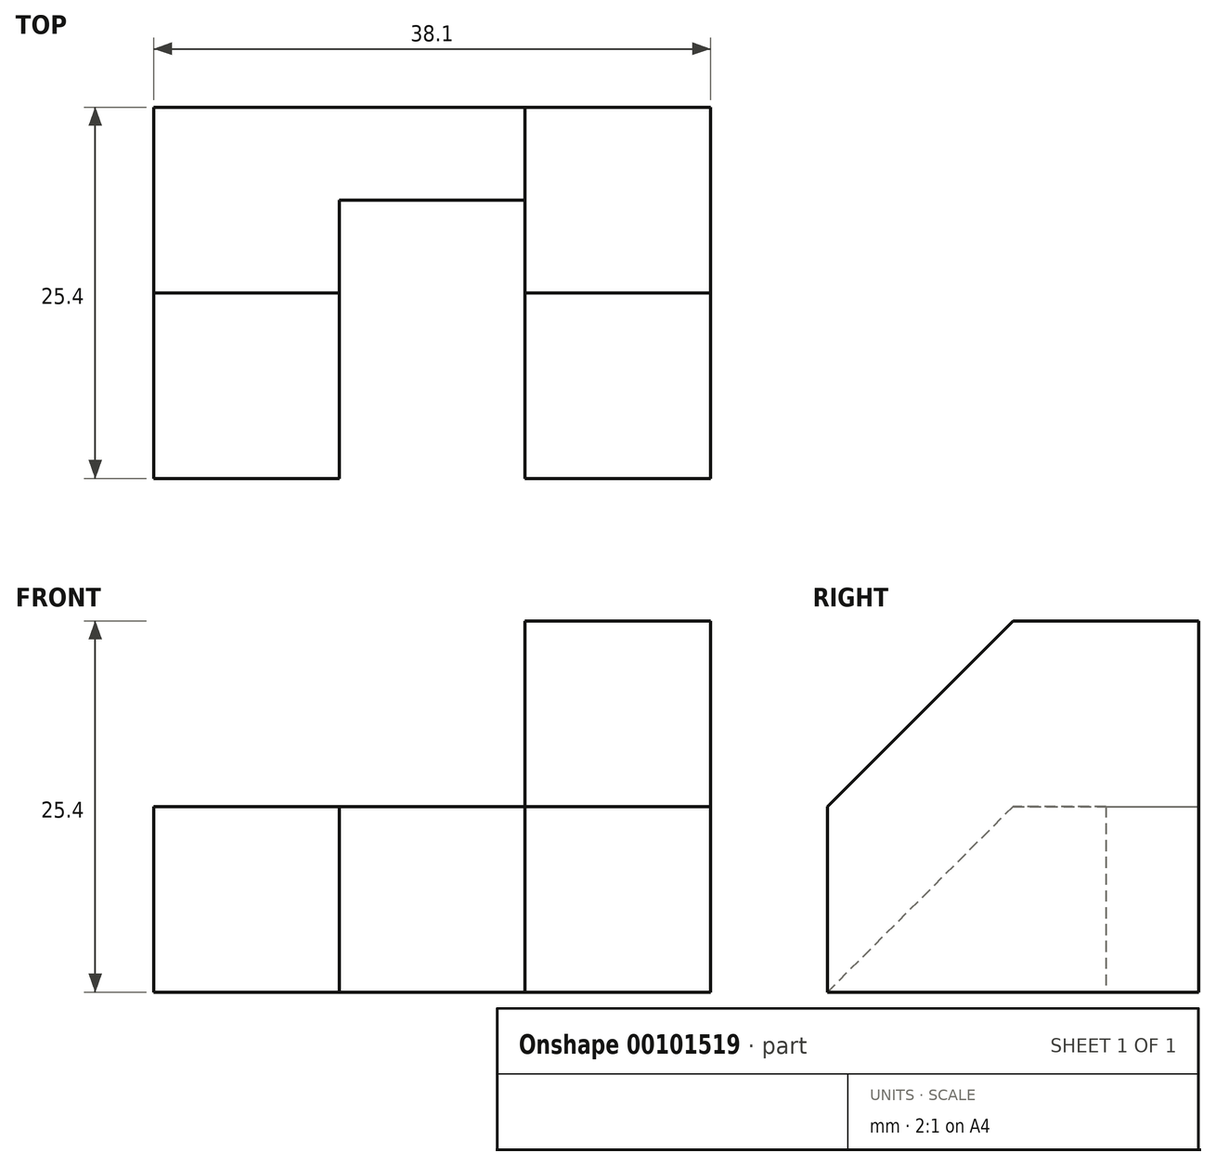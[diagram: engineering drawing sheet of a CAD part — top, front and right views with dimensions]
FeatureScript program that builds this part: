
annotation { "Feature Type Name" : "Feature", "Feature Type Description" : "" }
export const myFeature = defineFeature(function(context is Context, id is Id, definition is map)
    precondition{}
    {
        {
            var Q0;
            Q0=qCreatedBy(makeId("Top.planeOp"),FACE);
            var sketch = newSketch(context, id + "F0", { "sketchPlane" : qUnion([Q0])});
            skLineSegment(sketch, "E0.bottom", {"start": v(0, 0) * mm, "end": v(38.1, 0) * mm});
            skLineSegment(sketch, "E0.top", {"start": v(0, -25.4) * mm, "end": v(38.1, -25.4) * mm});
            skLineSegment(sketch, "E0.left", {"start": v(0, 0) * mm, "end": v(0, -25.4) * mm});
            skLineSegment(sketch, "E0.right", {"start": v(38.1, 0) * mm, "end": v(38.1, -25.4) * mm});
            skSolve(sketch);
        }
        {
            var Q0;
            Q0 = qSketchRegion(id + "F0", true);
            extrude(context, id + "F1", {"entities" : qUnion([Q0]), "depth" : 25.4 * mm});
        }
        {
            var Q0;
            Q0=qCreatedBy(makeId("Top.planeOp"),FACE);
            var sketch = newSketch(context, id + "F2", { "sketchPlane" : qUnion([Q0])});
            skLineSegment(sketch, "E1.bottom", {"start": v(0, 0) * mm, "end": v(12.7, 0) * mm});
            skLineSegment(sketch, "E1.top", {"start": v(0, -25.4) * mm, "end": v(12.7, -25.4) * mm});
            skLineSegment(sketch, "E1.left", {"start": v(0, 0) * mm, "end": v(0, -25.4) * mm});
            skLineSegment(sketch, "E1.right", {"start": v(12.7, 0) * mm, "end": v(12.7, -25.4) * mm});
            skLineSegment(sketch, "E2.bottom", {"start": v(12.7, -25.4) * mm, "end": v(25.4, -25.4) * mm});
            skLineSegment(sketch, "E2.top", {"start": v(12.7, -6.35) * mm, "end": v(25.4, -6.35) * mm});
            skLineSegment(sketch, "E2.left", {"start": v(12.7, -25.4) * mm, "end": v(12.7, -6.35) * mm});
            skLineSegment(sketch, "E2.right", {"start": v(25.4, -25.4) * mm, "end": v(25.4, -6.35) * mm});
            skSolve(sketch);
        }
        {
            var Q0;
            Q0=makeQuery(id+"F2.imprint","IMPRINT",FACE,{"disambiguationData":[TD([[makeQuery(id+"F2.imprint","IMPRINT",EDGE,{"derivedFrom":sQuery(id+"F2.wireOp",EDGE,"E2.bottom")}),1.0]])]});
            extrude(context, id + "F3", {"entities" : qUnion([Q0]), "operationType" : NewBodyOperationType.REMOVE, "endBound" : BoundingType.THROUGH_ALL, "depth" : 25.4 * mm});
        }
        {
            var Q0;
            Q0=qCreatedBy(makeId("Front.planeOp"),FACE);
            var sketch = newSketch(context, id + "F4", { "sketchPlane" : qUnion([Q0])});
            skLineSegment(sketch, "E3.bottom", {"start": v(0, 0) * mm, "end": v(25.4, 0) * mm});
            skLineSegment(sketch, "E3.top", {"start": v(0, 12.7) * mm, "end": v(25.4, 12.7) * mm});
            skLineSegment(sketch, "E3.left", {"start": v(0, 0) * mm, "end": v(0, 12.7) * mm});
            skLineSegment(sketch, "E3.right", {"start": v(25.4, 0) * mm, "end": v(25.4, 12.7) * mm});
            skLineSegment(sketch, "E4.top", {"start": v(0, 25.4) * mm, "end": v(25.4, 25.4) * mm});
            skLineSegment(sketch, "E4.left", {"start": v(0, 12.7) * mm, "end": v(0, 25.4) * mm});
            skLineSegment(sketch, "E4.right", {"start": v(25.4, 12.7) * mm, "end": v(25.4, 25.4) * mm});
            skSolve(sketch);
        }
        {
            var Q0;
            Q0=makeQuery(id+"F4.imprint","IMPRINT",FACE,{"disambiguationData":[TD([[makeQuery(id+"F4.imprint","IMPRINT",EDGE,{"derivedFrom":sQuery(id+"F4.wireOp",EDGE,"E3.top")}),1.0]])]});
            extrude(context, id + "F5", {"entities" : qUnion([Q0]), "operationType" : NewBodyOperationType.REMOVE, "endBound" : BoundingType.THROUGH_ALL, "depth" : 25.4 * mm});
        }
        {
            var Q0;
            Q0=qCreatedBy(makeId("Right.planeOp"),FACE);
            var sketch = newSketch(context, id + "F6", { "sketchPlane" : qUnion([Q0])});
            skLineSegment(sketch, "E5.bottom", {"start": v(0, 0) * mm, "end": v(-12.7, 0) * mm});
            skLineSegment(sketch, "E5.top", {"start": v(0, 12.7) * mm, "end": v(-12.7, 12.7) * mm});
            skLineSegment(sketch, "E5.left", {"start": v(0, 0) * mm, "end": v(0, 12.7) * mm});
            skLineSegment(sketch, "E5.right", {"start": v(-12.7, 0) * mm, "end": v(-12.7, 12.7) * mm});
            skLineSegment(sketch, "E6", {"start": v(-12.7, 12.7) * mm, "end": v(-25.4, 0) * mm});
            skLineSegment(sketch, "E7", {"start": v(-25.4, 0) * mm, "end": v(-25.4, 12.7) * mm});
            skLineSegment(sketch, "E8", {"start": v(-25.4, 12.7) * mm, "end": v(-12.7, 12.7) * mm});
            skSolve(sketch);
        }
        {
            var Q0;
            Q0=makeQuery(id+"F6.imprint","IMPRINT",FACE,{"disambiguationData":[TD([[makeQuery(id+"F6.imprint","IMPRINT",EDGE,{"derivedFrom":sQuery(id+"F6.wireOp",EDGE,"E6")}),-1.0]])]});
            extrude(context, id + "F7", {"entities" : qUnion([Q0]), "operationType" : NewBodyOperationType.REMOVE, "depth" : 12.7 * mm});
        }
        {
            var Q0;
            Q0=qCreatedBy(makeId("Right.planeOp"),FACE);
            var sketch = newSketch(context, id + "F8", { "sketchPlane" : qUnion([Q0])});
            skLineSegment(sketch, "E9.bottom", {"start": v(0, 0) * mm, "end": v(-12.7, 0) * mm});
            skLineSegment(sketch, "E9.top", {"start": v(0, 25.4) * mm, "end": v(-12.7, 25.4) * mm});
            skLineSegment(sketch, "E9.left", {"start": v(0, 0) * mm, "end": v(0, 25.4) * mm});
            skLineSegment(sketch, "E9.right", {"start": v(-12.7, 0) * mm, "end": v(-12.7, 25.4) * mm});
            skLineSegment(sketch, "E10.bottom", {"start": v(0, 0) * mm, "end": v(-25.4, 0) * mm});
            skLineSegment(sketch, "E10.top", {"start": v(0, 12.7) * mm, "end": v(-25.4, 12.7) * mm});
            skLineSegment(sketch, "E10.left", {"start": v(0, 0) * mm, "end": v(0, 12.7) * mm});
            skLineSegment(sketch, "E10.right", {"start": v(-25.4, 0) * mm, "end": v(-25.4, 12.7) * mm});
            skLineSegment(sketch, "E11", {"start": v(-25.4, 12.7) * mm, "end": v(-12.7, 25.4) * mm});
            skLineSegment(sketch, "E12", {"start": v(-12.7, 25.4) * mm, "end": v(-25.4, 25.4) * mm});
            skLineSegment(sketch, "E13", {"start": v(-25.4, 25.4) * mm, "end": v(-25.4, 12.7) * mm});
            skSolve(sketch);
        }
        {
            var Q0;
            Q0=makeQuery(id+"F8.imprint","IMPRINT",FACE,{"disambiguationData":[TD([[makeQuery(id+"F8.imprint","IMPRINT",EDGE,{"derivedFrom":sQuery(id+"F8.wireOp",EDGE,"E11")}),1.0]])]});
            extrude(context, id + "F9", {"entities" : qUnion([Q0]), "operationType" : NewBodyOperationType.REMOVE, "endBound" : BoundingType.THROUGH_ALL, "depth" : 25.4 * mm});
        }
    });
